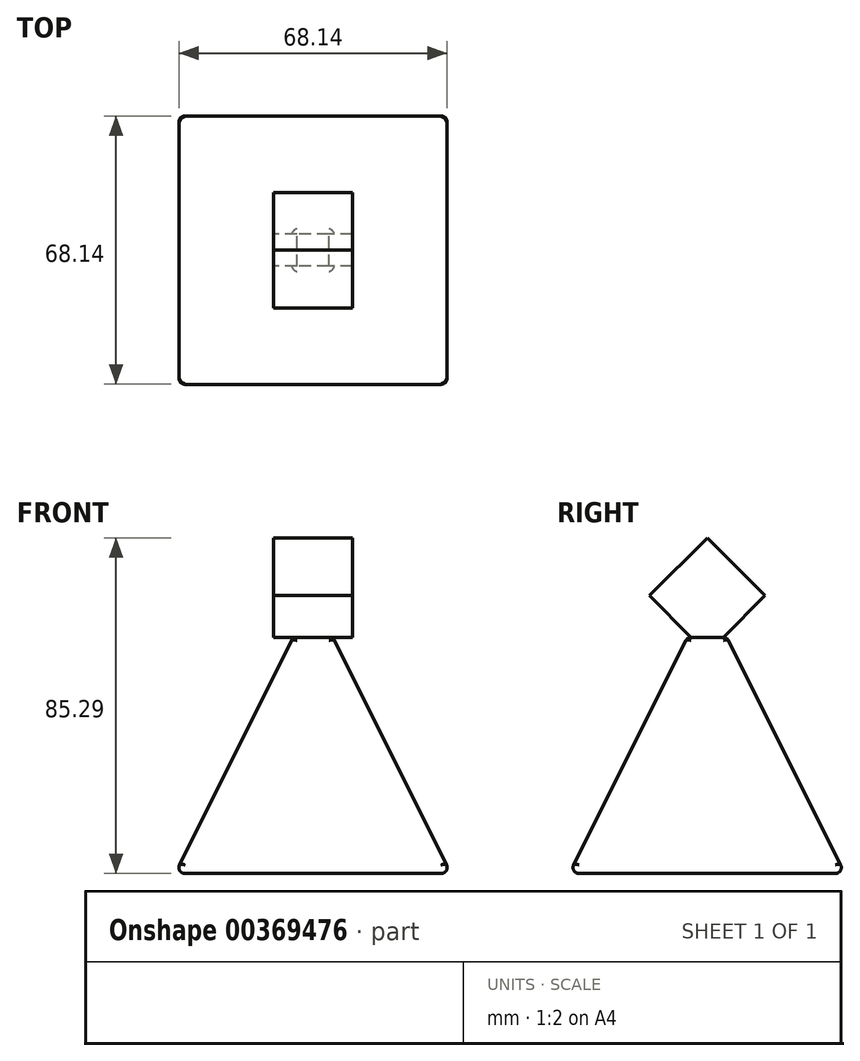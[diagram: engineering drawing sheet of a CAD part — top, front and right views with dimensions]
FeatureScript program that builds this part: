
annotation { "Feature Type Name" : "Feature", "Feature Type Description" : "" }
export const myFeature = defineFeature(function(context is Context, id is Id, definition is map)
    precondition{}
    {
        {
            var Q0;
            Q0=qCreatedBy(makeId("Top.planeOp"),FACE);
            var sketch = newSketch(context, id + "F0", { "sketchPlane" : qUnion([Q0])});
            skLineSegment(sketch, "E0.bottom", {"start": v(35, -35) * mm, "end": v(-35, -35) * mm});
            skLineSegment(sketch, "E0.top", {"start": v(35, 35) * mm, "end": v(-35, 35) * mm});
            skLineSegment(sketch, "E0.left", {"start": v(35, -35) * mm, "end": v(35, 35) * mm});
            skLineSegment(sketch, "E0.right", {"start": v(-35, -35) * mm, "end": v(-35, 35) * mm});
            skPoint(sketch, "E0.middle", {"position": v(0, 0) * mm});
            skSolve(sketch);
        }
        {
            var Q0;
            Q0=qCreatedBy(makeId("Top.planeOp"),FACE);
            cPlane(context, id + "F1", {"entities" : qUnion([Q0]), "cplaneType" : CPlaneType.OFFSET, "offset" : 60 * mm, "width" : 150 * mm, "height" : 150 * mm});
        }
        {
            var Q0;
            Q0=qCreatedBy(id+"F1.planeOp",FACE);
            var sketch = newSketch(context, id + "F2", { "sketchPlane" : qUnion([Q0])});
            skLineSegment(sketch, "E1.bottom", {"start": v(5, -5) * mm, "end": v(-5, -5) * mm});
            skLineSegment(sketch, "E1.top", {"start": v(5, 5) * mm, "end": v(-5, 5) * mm});
            skLineSegment(sketch, "E1.left", {"start": v(5, -5) * mm, "end": v(5, 5) * mm});
            skLineSegment(sketch, "E1.right", {"start": v(-5, -5) * mm, "end": v(-5, 5) * mm});
            skPoint(sketch, "E1.middle", {"position": v(0, 0) * mm});
            skSolve(sketch);
        }
        {
            var Q0;
            Q0 = qSketchRegion(id + "F0", true);
            var Q1;
            Q1 = qSketchRegion(id + "F2", true);
            loft(context, id + "F3", {"sheetProfilesArray" : [{ "sheetProfileEntities" : qUnion([Q0]) }, { "sheetProfileEntities" : qUnion([Q1]) }]});
        }
        {
            var Q0;
            Q0=makeQuery(id+"F3.opLoft","SWEPT_FACE",FACE,{"disambiguationData":[OSD([sQuery(id+"F0.wireOp",EDGE,"E0.bottom"),sQuery(id+"F0.wireOp",EDGE,"E0.top"),sQuery(id+"F0.wireOp",EDGE,"E0.left"),sQuery(id+"F2.wireOp",EDGE,"E1.bottom"),sQuery(id+"F2.wireOp",EDGE,"E1.top"),sQuery(id+"F2.wireOp",EDGE,"E1.left")])]});
            var Q1;
            Q1=makeQuery(id+"F3.opLoft","SWEPT_FACE",FACE,{"disambiguationData":[OSD([sQuery(id+"F0.wireOp",EDGE,"E0.bottom"),sQuery(id+"F0.wireOp",EDGE,"E0.left"),sQuery(id+"F0.wireOp",EDGE,"E0.right"),sQuery(id+"F2.wireOp",EDGE,"E1.bottom"),sQuery(id+"F2.wireOp",EDGE,"E1.left"),sQuery(id+"F2.wireOp",EDGE,"E1.right")])]});
            var Q2;
            Q2=makeQuery(id+"F3.opLoft","SWEPT_FACE",FACE,{"disambiguationData":[OSD([sQuery(id+"F0.wireOp",EDGE,"E0.bottom"),sQuery(id+"F0.wireOp",EDGE,"E0.top"),sQuery(id+"F0.wireOp",EDGE,"E0.right"),sQuery(id+"F2.wireOp",EDGE,"E1.bottom"),sQuery(id+"F2.wireOp",EDGE,"E1.top"),sQuery(id+"F2.wireOp",EDGE,"E1.right")])]});
            var Q3;
            Q3=makeQuery(id+"F3.opLoft","SWEPT_FACE",FACE,{"disambiguationData":[OSD([sQuery(id+"F0.wireOp",EDGE,"E0.top"),sQuery(id+"F0.wireOp",EDGE,"E0.left"),sQuery(id+"F0.wireOp",EDGE,"E0.right"),sQuery(id+"F2.wireOp",EDGE,"E1.top"),sQuery(id+"F2.wireOp",EDGE,"E1.left"),sQuery(id+"F2.wireOp",EDGE,"E1.right")])]});
            fillet(context, id + "F4", {"entities" : qUnion([Q0, Q1, Q2, Q3]), "radius" : 1.5 * mm, "tangentPropagation" : true, "allowEdgeOverflow" : false});
        }
        {
            var Q0;
            Q0=qCreatedBy(makeId("Right.planeOp"),FACE);
            var sketch = newSketch(context, id + "F5", { "sketchPlane" : qUnion([Q0])});
            skLineSegment(sketch, "E2.0.0", {"start": v(4.07, 59.17) * mm, "end": v(4.07, 60) * mm});
            skLineSegment(sketch, "E2.0.1", {"start": v(4.07, 60) * mm, "end": v(-4.07, 60) * mm});
            skPoint(sketch, "E2.0.2.end.orphan", {"position": v(-4.07, 59.17) * mm});
            skLineSegment(sketch, "E3", {"start": v(-4.07, 60) * mm, "end": v(-14.68, 70.6) * mm});
            skLineSegment(sketch, "E4", {"start": v(-14.68, 70.6) * mm, "end": v(0, 85.29) * mm});
            skLineSegment(sketch, "E5", {"start": v(4.07, 60) * mm, "end": v(14.68, 70.6) * mm});
            skLineSegment(sketch, "E6", {"start": v(0, 85.29) * mm, "end": v(14.68, 70.6) * mm});
            skSolve(sketch);
        }
        {
            var Q0;
            Q0 = qSketchRegion(id + "F5", true);
            extrude(context, id + "F6", {"entities" : qUnion([Q0]), "operationType" : NewBodyOperationType.ADD, "endBound" : BoundingType.SYMMETRIC, "depth" : 20 * mm});
        }
    });
